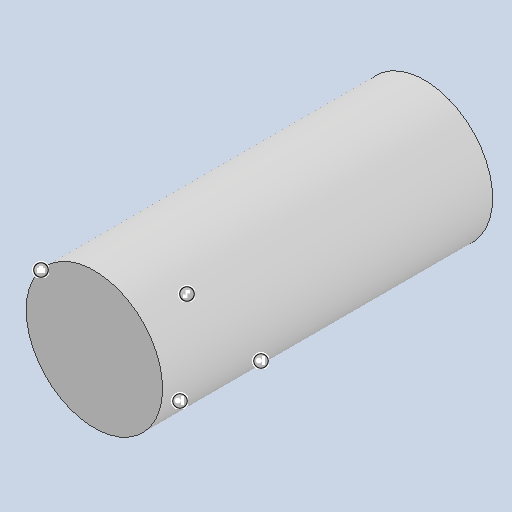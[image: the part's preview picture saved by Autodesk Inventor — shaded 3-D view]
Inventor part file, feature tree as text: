
AUTODESK INVENTOR PART (.ipt)
format: ipt  version: 2024.2 (Build 282272000, 272)  size: 205,824 bytes
history: native  units: mm
features: extrude x1
ambient origin geometry x8: Origin, YZ Plane, XZ Plane, XY Plane, X Axis, Y Axis, Z Axis, Center Point
bodies: Solid1 (feature_tree)
feature tree (1):
  extrude  "Extrusion1"  TaperAngle=0.0deg  [1 undecoded]
note: 1 required parameter value undecoded (feature->parameter linkage not recoverable at this tier; creation-order binding heuristic only, values carry confidence <= 0.55)
